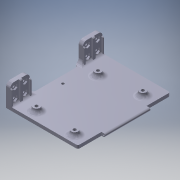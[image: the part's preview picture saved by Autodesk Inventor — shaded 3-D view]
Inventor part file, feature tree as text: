
AUTODESK INVENTOR PART (.ipt)
format: ipt  version: 2018 (Build 220112000, 112)  size: 554,496 bytes
history: native  units: mm
features: extrude x13, sketch x12, other x6, projected_geometry x4, reference x3, fillet x2, imported_body x1
ambient origin geometry x8: Origin, YZ Plane, XZ Plane, XY Plane, X Axis, Y Axis, Z Axis, Center Point
bodies: Solid1 (feature_tree)
feature tree (41):
  extrude  "Extrusion1"  Depth=10.0mm TaperAngle=0.0deg
  extrude  "Extrusion2"  Depth=10.0mm TaperAngle=0.0deg
  extrude  "Extrusion3"  Depth=3.0mm
  extrude  "Extrusion4"  Depth=5.8mm
  extrude  "Extrusion5"  Depth=5.8mm
  extrude  "Extrusion6"  Depth=5.8mm
  extrude  "Extrusion7"  Depth=2.8mm TaperAngle=0.0deg
  extrude  "Extrusion8"  Depth=10.0mm TaperAngle=0.0deg
  extrude  "Extrusion9"  Depth=10.0mm TaperAngle=0.0deg
  fillet  "Fillet1"  Radius=2.0mm
  extrude  "Extrusion10"  Depth=10.0mm TaperAngle=0.0deg
  fillet  "Fillet2"  Radius=10.0mm
  extrude  "Extrusion11"  Depth=10.0mm TaperAngle=0.0deg
  extrude  "Extrusion13"  Depth=9.0mm
  extrude  "Extrusion14"  Depth=4.0mm
  sketch  "Sketch1"  dims[d0=10.0mm d1=0.0mm d2=10.0mm d3=0.0mm]
  sketch  "Sketch2"  dims[d4=10.0mm d5=0.0mm d6=10.0mm d7=0.0mm]
  sketch  "Sketch3"  dims[d8=10.0mm d9=0.0mm d10=3.0mm]
  projected_geometry  "Projected Loop3"
  sketch  "Sketch4"  dims[d11=10.0mm d12=0.0mm d13=5.8mm]
  sketch  "Sketch6"  dims[d14=2.0mm d15=5.0mm d16=0.0mm d17=0.0mm d18=5.8mm]
  sketch  "Sketch7"  dims[d19=5.8mm d20=5.8mm]
  projected_geometry  "Projected Loop4"
  projected_geometry  "Projected Loop5"
  sketch  "Sketch8"  dims[d21=5.8mm d22=2.8mm d23=0.0mm]
  projected_geometry  "Projected Loop6"
  sketch  "Sketch10"  dims[d24=3.8mm d25=10.0mm d26=0.0mm]
  sketch  "Sketch11"  dims[d27=5.0mm d29=10.0mm d30=0.0mm d31=2.0mm]
  reference  "Reference3"
  sketch  "Sketch12"  dims[d33=55.0mm d34=10.0mm d35=0.0mm d41=10.0mm d42=0.0mm]
  sketch  "Sketch14"  dims[d43=3.2mm d44=10.0mm d45=0.0mm]
  sketch  "Sketch15"  dims[d46=6.0mm d47=9.0mm d48=4.0mm d49=1.8mm]
  reference  "Reference4"
  reference  "Reference5"
  imported_body  "Base1"
  other  "<userpath>\Downloads\git_WSL\MEME_MACHINE\CAD\RAMPS Mount\RAMPS Mount.iam"
  other  "RAMPS Mount.iam"
  other  "Arduino RAMPS combo:1"
  other  "RAMPS1_4_1"
  other  "ARDUINO_MEGA_45"
  other  "ARDUINO_MEGA_BRD_74"
